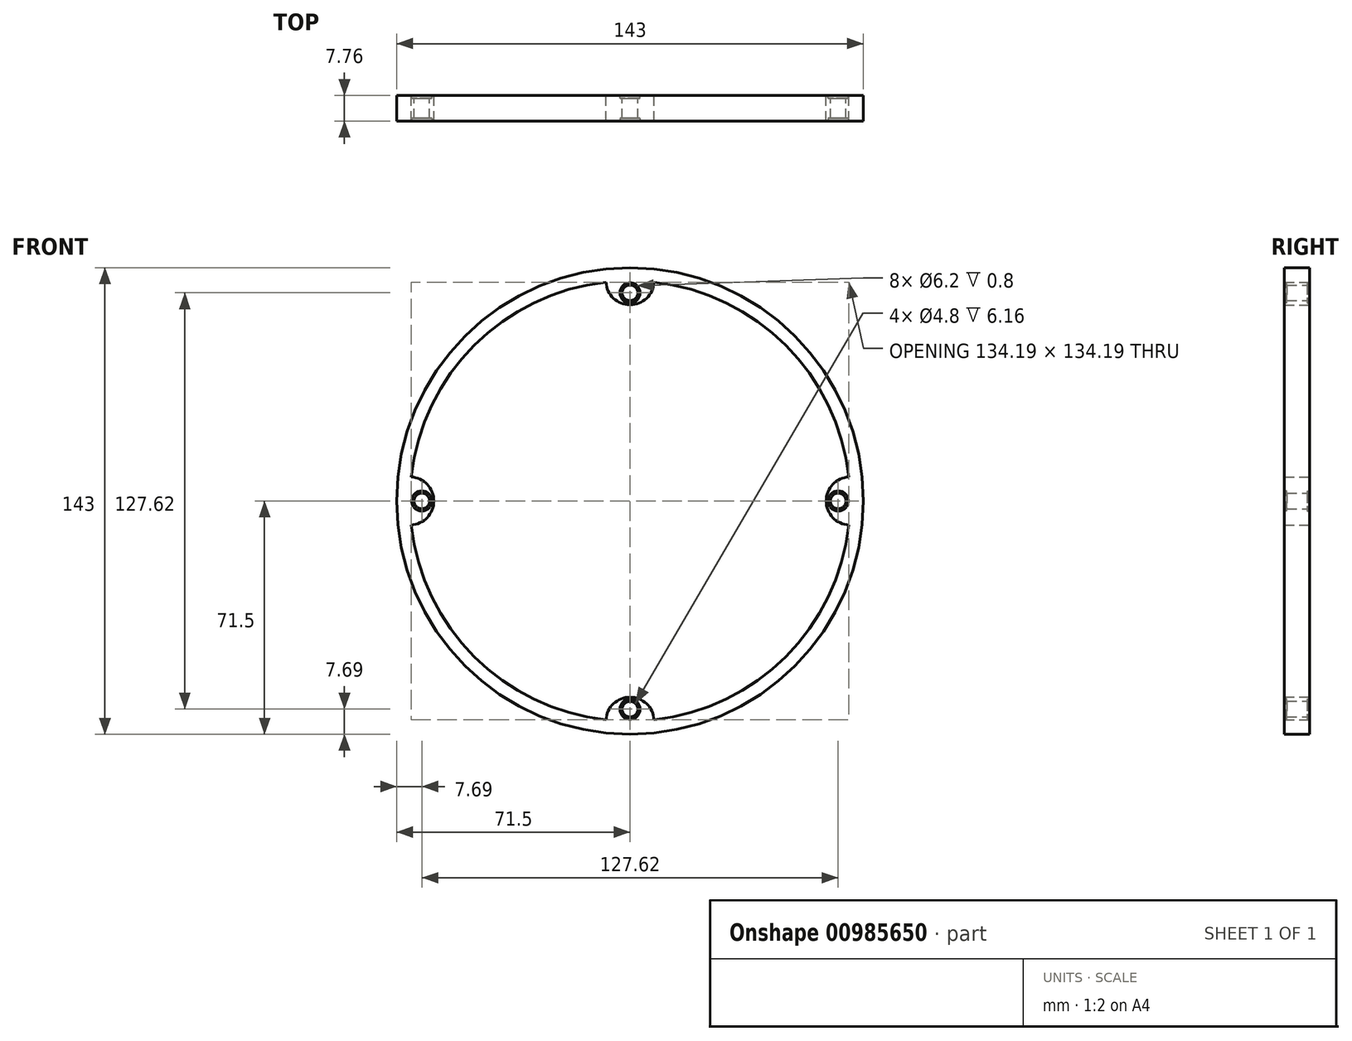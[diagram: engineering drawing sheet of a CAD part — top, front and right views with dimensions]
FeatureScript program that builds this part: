
annotation { "Feature Type Name" : "Feature", "Feature Type Description" : "" }
export const myFeature = defineFeature(function(context is Context, id is Id, definition is map)
    precondition{}
    {
        {
            var Q0;
            Q0=qCreatedBy(makeId("Front.planeOp"),FACE);
            var sketch = newSketch(context, id + "F0", { "sketchPlane" : qUnion([Q0])});
            skCircle(sketch, "E0", {"center": v(0, 0) * mm, "radius": 71.5 * mm});
            skArc(sketch, "E1", {"start": v(-7.37, 67.1) * mm, "mid": v(-47.73, 47.73) * mm, "end": v(-67.1, 7.37) * mm});
            skCircle(sketch, "E2", {"center": v(0, 0) * mm, "radius": 60.12 * mm, "construction": true});
            skArc(sketch, "E3", {"start": v(-7.37, 67.1) * mm, "mid": v(0, 60.12) * mm, "end": v(7.37, 67.1) * mm});
            skLineSegment(sketch, "E4", {"start": v(0, 67.5) * mm, "end": v(0, 60.12) * mm, "construction": true});
            skPoint(sketch, "E5", {"position": v(0, 63.81) * mm});
            skCircle(sketch, "E6", {"center": v(0, 63.81) * mm, "radius": 2.4 * mm});
            skArc(sketch, "E7", {"start": v(67.1, 7.37) * mm, "mid": v(60.12, 0) * mm, "end": v(67.1, -7.37) * mm});
            skArc(sketch, "E8", {"start": v(7.37, -67.1) * mm, "mid": v(0, -60.12) * mm, "end": v(-7.37, -67.1) * mm});
            skArc(sketch, "E9", {"start": v(-67.1, -7.37) * mm, "mid": v(-60.12, 0) * mm, "end": v(-67.1, 7.37) * mm});
            skArc(sketch, "E10.trimOffspring", {"start": v(67.1, 7.37) * mm, "mid": v(47.73, 47.73) * mm, "end": v(7.37, 67.1) * mm});
            skArc(sketch, "E11.trimOffspring", {"start": v(7.37, -67.1) * mm, "mid": v(47.73, -47.73) * mm, "end": v(67.1, -7.37) * mm});
            skArc(sketch, "E12.trimOffspring", {"start": v(-67.1, -7.37) * mm, "mid": v(-47.73, -47.73) * mm, "end": v(-7.37, -67.1) * mm});
            skLineSegment(sketch, "E13", {"start": v(67.5, 0) * mm, "end": v(60.12, 0) * mm, "construction": true});
            skLineSegment(sketch, "E14", {"start": v(0, -67.5) * mm, "end": v(0, -60.12) * mm, "construction": true});
            skLineSegment(sketch, "E15", {"start": v(-67.5, 0) * mm, "end": v(-60.12, 0) * mm, "construction": true});
            skPoint(sketch, "E16", {"position": v(63.81, 0) * mm});
            skPoint(sketch, "E17", {"position": v(0, -63.81) * mm});
            skPoint(sketch, "E18", {"position": v(-63.81, 0) * mm});
            skCircle(sketch, "E19", {"center": v(63.81, 0) * mm, "radius": 2.4 * mm});
            skCircle(sketch, "E20", {"center": v(0, -63.81) * mm, "radius": 2.4 * mm});
            skCircle(sketch, "E21", {"center": v(-63.81, 0) * mm, "radius": 2.4 * mm});
            skSolve(sketch);
        }
        {
            var Q0;
            Q0=makeQuery(id+"F0.imprint","IMPRINT",FACE,{"disambiguationData":[TD([[makeQuery(id+"F0.imprint","IMPRINT",EDGE,{"derivedFrom":sQuery(id+"F0.wireOp",EDGE,"E0")}),1.0]])]});
            extrude(context, id + "F1", {"entities" : qUnion([Q0]), "endBound" : BoundingType.SYMMETRIC, "depth" : 7.76 * mm, "offsetDistance" : 25 * mm});
        }
        {
            var Q0;
            Q0=makeQuery(id+"F1.opExtrude","CAP_FACE",FACE,{"disambiguationData":[OSD([sQuery(id+"F0.wireOp",EDGE,"E0"),sQuery(id+"F0.wireOp",EDGE,"E1"),sQuery(id+"F0.wireOp",EDGE,"E3"),sQuery(id+"F0.wireOp",EDGE,"E6"),sQuery(id+"F0.wireOp",EDGE,"E7"),sQuery(id+"F0.wireOp",EDGE,"E8"),sQuery(id+"F0.wireOp",EDGE,"E9"),sQuery(id+"F0.wireOp",EDGE,"E10.trimOffspring"),sQuery(id+"F0.wireOp",EDGE,"E11.trimOffspring"),sQuery(id+"F0.wireOp",EDGE,"E12.trimOffspring"),sQuery(id+"F0.wireOp",EDGE,"E19"),sQuery(id+"F0.wireOp",EDGE,"E20"),sQuery(id+"F0.wireOp",EDGE,"E21")])],"isStart":false});
            var sketch = newSketch(context, id + "F2", { "sketchPlane" : qUnion([Q0])});
            skCircle(sketch, "E22", {"center": v(0, 63.81) * mm, "radius": 3.1 * mm});
            skCircle(sketch, "E23", {"center": v(63.81, 0) * mm, "radius": 3.1 * mm});
            skCircle(sketch, "E24", {"center": v(0, -63.81) * mm, "radius": 3.1 * mm});
            skCircle(sketch, "E25", {"center": v(-63.81, 0) * mm, "radius": 3.1 * mm});
            skSolve(sketch);
        }
        {
            var Q0;
            Q0 = qSketchRegion(id + "F2", true);
            extrude(context, id + "F3", {"entities" : qUnion([Q0]), "operationType" : NewBodyOperationType.REMOVE, "oppositeDirection" : true, "depth" : .8 * mm, "offsetDistance" : 25 * mm});
        }
        {
            var Q0;
            Q0=makeQuery(id+"F1.opExtrude","CAP_FACE",FACE,{"disambiguationData":[OSD([sQuery(id+"F0.wireOp",EDGE,"E0"),sQuery(id+"F0.wireOp",EDGE,"E1"),sQuery(id+"F0.wireOp",EDGE,"E3"),sQuery(id+"F0.wireOp",EDGE,"E6"),sQuery(id+"F0.wireOp",EDGE,"E7"),sQuery(id+"F0.wireOp",EDGE,"E8"),sQuery(id+"F0.wireOp",EDGE,"E9"),sQuery(id+"F0.wireOp",EDGE,"E10.trimOffspring"),sQuery(id+"F0.wireOp",EDGE,"E11.trimOffspring"),sQuery(id+"F0.wireOp",EDGE,"E12.trimOffspring"),sQuery(id+"F0.wireOp",EDGE,"E19"),sQuery(id+"F0.wireOp",EDGE,"E20"),sQuery(id+"F0.wireOp",EDGE,"E21")])],"isStart":true});
            var sketch = newSketch(context, id + "F4", { "sketchPlane" : qUnion([Q0])});
            skCircle(sketch, "E26", {"center": v(0, 63.81) * mm, "radius": 3.1 * mm});
            skCircle(sketch, "E27", {"center": v(63.81, 0) * mm, "radius": 3.1 * mm});
            skCircle(sketch, "E28", {"center": v(0, -63.81) * mm, "radius": 3.1 * mm});
            skCircle(sketch, "E29", {"center": v(-63.81, 0) * mm, "radius": 3.1 * mm});
            skSolve(sketch);
        }
        {
            var Q0;
            Q0 = qSketchRegion(id + "F4", true);
            extrude(context, id + "F5", {"entities" : qUnion([Q0]), "operationType" : NewBodyOperationType.REMOVE, "oppositeDirection" : true, "depth" : .8 * mm, "offsetDistance" : 25 * mm});
        }
    });
